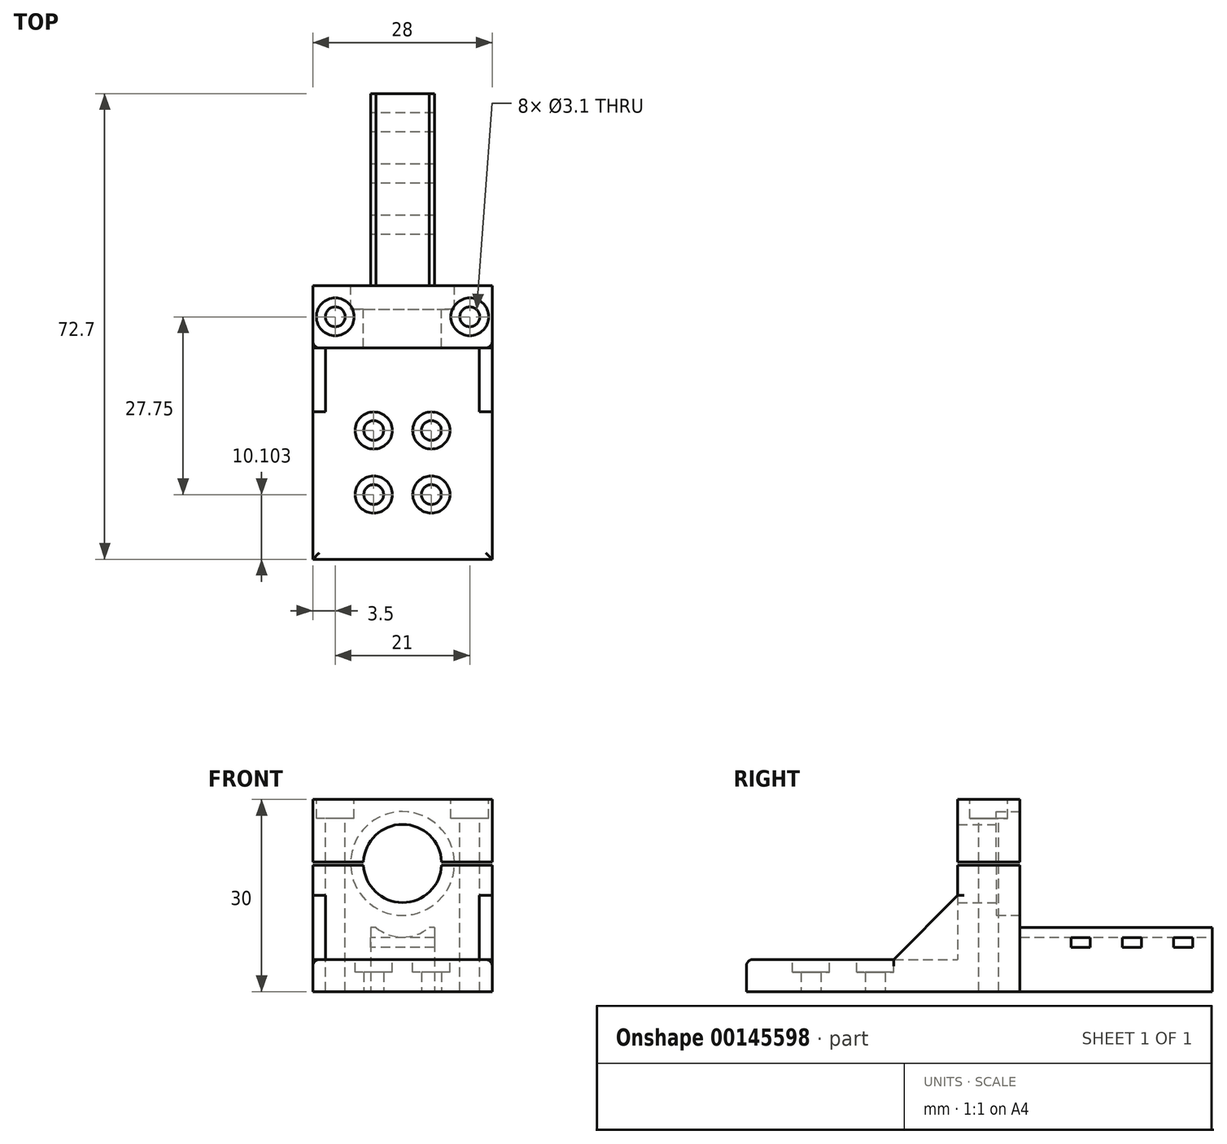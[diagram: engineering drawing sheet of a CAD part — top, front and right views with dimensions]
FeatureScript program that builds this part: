
annotation { "Feature Type Name" : "Feature", "Feature Type Description" : "" }
export const myFeature = defineFeature(function(context is Context, id is Id, definition is map)
    precondition{}
    {
        {
            var Q0;
            Q0=qCreatedBy(makeId("Top.planeOp"),FACE);
            var sketch = newSketch(context, id + "F0", { "sketchPlane" : qUnion([Q0])});
            skLineSegment(sketch, "E0", {"start": v(-14, 6.1) * mm, "end": v(-14, -26.9) * mm});
            skLineSegment(sketch, "E1", {"start": v(-14, -26.9) * mm, "end": v(14, -26.9) * mm});
            skLineSegment(sketch, "E2", {"start": v(14, -26.9) * mm, "end": v(14, 6.1) * mm});
            skLineSegment(sketch, "E3", {"start": v(14, 15.8) * mm, "end": v(-14, 15.8) * mm});
            skLineSegment(sketch, "E4.bottom", {"start": v(4.5, -6.8) * mm, "end": v(-4.5, -6.8) * mm, "construction": true});
            skLineSegment(sketch, "E4.top", {"start": v(4.5, -16.8) * mm, "end": v(-4.5, -16.8) * mm, "construction": true});
            skLineSegment(sketch, "E4.left", {"start": v(4.5, -6.8) * mm, "end": v(4.5, -16.8) * mm, "construction": true});
            skLineSegment(sketch, "E4.right", {"start": v(-4.5, -6.8) * mm, "end": v(-4.5, -16.8) * mm, "construction": true});
            skPoint(sketch, "E4.middle", {"position": v(0, -11.8) * mm});
            skCircle(sketch, "E5", {"center": v(-4.5, -6.8) * mm, "radius": 1.55 * mm});
            skCircle(sketch, "E6", {"center": v(4.5, -6.8) * mm, "radius": 1.55 * mm});
            skCircle(sketch, "E7", {"center": v(-4.5, -16.8) * mm, "radius": 1.55 * mm});
            skCircle(sketch, "E8", {"center": v(4.5, -16.8) * mm, "radius": 1.55 * mm});
            skLineSegment(sketch, "E9", {"start": v(-14, 6.1) * mm, "end": v(14, 6.1) * mm});
            skCircle(sketch, "E10", {"center": v(-10.5, 10.95) * mm, "radius": 1.3 * mm});
            skCircle(sketch, "E11", {"center": v(10.5, 10.95) * mm, "radius": 1.3 * mm});
            skLineSegment(sketch, "E12", {"start": v(-14, 6.1) * mm, "end": v(-12, 6.1) * mm});
            skLineSegment(sketch, "E13", {"start": v(-12, 6.1) * mm, "end": v(-12, -3.9) * mm});
            skLineSegment(sketch, "E14", {"start": v(-12, -3.9) * mm, "end": v(-14, -3.9) * mm});
            skLineSegment(sketch, "E15", {"start": v(14, 6.1) * mm, "end": v(12, 6.1) * mm});
            skLineSegment(sketch, "E16", {"start": v(12, 6.1) * mm, "end": v(12, -3.9) * mm});
            skLineSegment(sketch, "E17", {"start": v(12, -3.9) * mm, "end": v(14, -3.9) * mm});
            skLineSegment(sketch, "E18", {"start": v(-14, 15.8) * mm, "end": v(-14, 6.1) * mm});
            skLineSegment(sketch, "E19", {"start": v(14, 15.8) * mm, "end": v(14, 6.1) * mm});
            skPoint(sketch, "E20", {"position": v(-14, 10.95) * mm});
            skLineSegment(sketch, "E21", {"start": v(-14, 10.95) * mm, "end": v(14, 10.95) * mm, "construction": true});
            skLineSegment(sketch, "E22", {"start": v(0, 38.9) * mm, "end": v(0, -44.05) * mm, "construction": true});
            skLineSegment(sketch, "E23.bottom", {"start": v(-5, 45.8) * mm, "end": v(5, 45.8) * mm});
            skLineSegment(sketch, "E23.top", {"start": v(-5, 15.8) * mm, "end": v(5, 15.8) * mm});
            skLineSegment(sketch, "E23.left", {"start": v(-5, 45.8) * mm, "end": v(-5, 15.8) * mm});
            skLineSegment(sketch, "E23.right", {"start": v(5, 45.8) * mm, "end": v(5, 15.8) * mm});
            skPoint(sketch, "E23.middle", {"position": v(0, 30.8) * mm});
            skSolve(sketch);
        }
        {
            var Q0;
            {var subQ2=sQuery(id+"F0.wireOp",EDGE,"E1");Q0=makeQuery(id+"F0.imprint","IMPRINT",FACE,{"disambiguationData":[TD([[makeQuery(id+"F0.imprint","IMPRINT",EDGE,{"derivedFrom":subQ2}),1.0]])]});}
            var Q1;
            {var subQ2=sQuery(id+"F0.wireOp",EDGE,"E12");Q1=makeQuery(id+"F0.imprint","IMPRINT",FACE,{"disambiguationData":[TD([[makeQuery(id+"F0.imprint","IMPRINT",EDGE,{"derivedFrom":subQ2}),-1.0]])]});}
            var Q2;
            {var subQ0=sQuery(id+"F0.wireOp",EDGE,"E15");Q2=makeQuery(id+"F0.imprint","IMPRINT",FACE,{"disambiguationData":[TD([[makeQuery(id+"F0.imprint","IMPRINT",EDGE,{"derivedFrom":subQ0}),1.0]])]});}
            var Q3;
            {var subQ4=sQuery(id+"F0.wireOp",EDGE,"c3Up1kXt-IVpb-vE7n-Jt2L-Xucas93thEKn");Q3=makeQuery(id+"F0.imprint","IMPRINT",FACE,{"disambiguationData":[TD([[makeQuery(id+"F0.imprint","IMPRINT",EDGE,{"derivedFrom":subQ4}),1.0]])]});}
            var Q4;
            {var subQ4=sQuery(id+"F0.wireOp",EDGE,"E13");Q4=makeQuery(id+"F0.imprint","IMPRINT",FACE,{"disambiguationData":[TD([[makeQuery(id+"F0.imprint","IMPRINT",EDGE,{"derivedFrom":subQ4}),-1.0]])]});}
            var Q5;
            {var subQ4=sQuery(id+"F0.wireOp",EDGE,"E16");Q5=makeQuery(id+"F0.imprint","IMPRINT",FACE,{"disambiguationData":[TD([[makeQuery(id+"F0.imprint","IMPRINT",EDGE,{"derivedFrom":subQ4}),1.0]])]});}
            extrude(context, id + "F1", {"entities" : qUnion([Q0, Q1, Q2, Q3, Q4, Q5]), "depth" : 5 * mm, "offsetDistance" : 25 * mm});
        }
        {
            var Q0;
            {var subQ4=sQuery(id+"F0.wireOp",EDGE,"E13");Q0=makeQuery(id+"F0.imprint","IMPRINT",FACE,{"disambiguationData":[TD([[makeQuery(id+"F0.imprint","IMPRINT",EDGE,{"derivedFrom":subQ4}),-1.0]])]});}
            var Q1;
            {var subQ4=sQuery(id+"F0.wireOp",EDGE,"E16");Q1=makeQuery(id+"F0.imprint","IMPRINT",FACE,{"disambiguationData":[TD([[makeQuery(id+"F0.imprint","IMPRINT",EDGE,{"derivedFrom":subQ4}),1.0]])]});}
            extrude(context, id + "F2", {"entities" : qUnion([Q0, Q1]), "operationType" : NewBodyOperationType.ADD, "depth" : 15 * mm, "offsetDistance" : 25 * mm});
        }
        {
            var Q0;
            Q0=makeQuery(id+"F0.imprint","IMPRINT",FACE,{"disambiguationData":[TD([[makeQuery(id+"F0.imprint","IMPRINT",EDGE,{"derivedFrom":sQuery(id+"F0.wireOp",EDGE,"E3")}),1.0]])]});
            extrude(context, id + "F3", {"entities" : qUnion([Q0]), "operationType" : NewBodyOperationType.ADD, "depth" : 30 * mm, "offsetDistance" : 25 * mm});
        }
        {
            var Q0;
            Q0=makeQuery(id+"F3.opExtrude","SWEPT_FACE",FACE,{"disambiguationData":[OSD([sQuery(id+"F0.wireOp",EDGE,"E3")])]});
            var sketch = newSketch(context, id + "F4", { "sketchPlane" : qUnion([Q0])});
            skLineSegment(sketch, "E24", {"start": v(14, 20) * mm, "end": v(-14, 20) * mm, "construction": true});
            skPoint(sketch, "E24.endSnap0", {"position": v(-14, 15) * mm});
            skLineSegment(sketch, "E25", {"start": v(14, 20.25) * mm, "end": v(-14, 20.25) * mm});
            skLineSegment(sketch, "E26", {"start": v(14, 19.75) * mm, "end": v(-14, 19.75) * mm});
            skCircle(sketch, "E27", {"center": v(0, 20) * mm, "radius": 6.1 * mm});
            skCircle(sketch, "E28", {"center": v(0, 20) * mm, "radius": 8.1 * mm});
            skPoint(sketch, "E29.0", {"position": v(0, 0) * mm});
            skLineSegment(sketch, "E30", {"start": v(0, 0) * mm, "end": v(0, 30) * mm, "construction": true});
            skLineSegment(sketch, "E31.0", {"start": v(14, 5) * mm, "end": v(-14, 5) * mm, "construction": true});
            skSolve(sketch);
        }
        {
            var Q0;
            {var subQ0=sQuery(id+"F4.wireOp",EDGE,"E25");var subQ3=sQuery(id+"F4.wireOp",EDGE,"MANSPHcc-LTuF-cz86-WJFN-Q4U81JYctoWT");var subQ4=makeQuery(id+"F4.imprint","INTERSECT",VERTEX,{"derivedFrom":[subQ0,subQ3]});Q0=makeQuery(id+"F4.imprint","IMPRINT",FACE,{"disambiguationData":[TD([[makeQuery(id+"F4.imprint","IMPRINT",EDGE,{"disambiguationData":[TD([[subQ4,-1.0]])],"derivedFrom":subQ3}),1.0]])]});}
            var Q1;
            {var subQ0=sQuery(id+"F4.wireOp",EDGE,"E27");var subQ1=sQuery(id+"F4.wireOp",EDGE,"E25");var subQ2=makeQuery(id+"F4.imprint","INTERSECT",VERTEX,{"disambiguationData":[OD(0.0)],"derivedFrom":[subQ1,subQ0]});Q1=makeQuery(id+"F4.imprint","IMPRINT",FACE,{"disambiguationData":[TD([[makeQuery(id+"F4.imprint","IMPRINT",EDGE,{"disambiguationData":[TD([[subQ2,-1.0]])],"derivedFrom":subQ1}),-1.0]])]});}
            var Q2;
            {var subQ0=sQuery(id+"F4.wireOp",EDGE,"E27");var subQ1=sQuery(id+"F4.wireOp",EDGE,"E26");var subQ2=makeQuery(id+"F4.imprint","INTERSECT",VERTEX,{"disambiguationData":[OD(0.0)],"derivedFrom":[subQ1,subQ0]});Q2=makeQuery(id+"F4.imprint","IMPRINT",FACE,{"disambiguationData":[TD([[makeQuery(id+"F4.imprint","IMPRINT",EDGE,{"disambiguationData":[TD([[subQ2,-1.0]])],"derivedFrom":subQ1}),1.0]])]});}
            var Q3;
            {var subQ0=sQuery(id+"F4.wireOp",EDGE,"E27");var subQ1=sQuery(id+"F4.wireOp",EDGE,"E25");var subQ2=makeQuery(id+"F4.imprint","INTERSECT",VERTEX,{"disambiguationData":[OD(0.0)],"derivedFrom":[subQ1,subQ0]});Q3=makeQuery(id+"F4.imprint","IMPRINT",FACE,{"disambiguationData":[TD([[makeQuery(id+"F4.imprint","IMPRINT",EDGE,{"disambiguationData":[TD([[subQ2,-1.0]])],"derivedFrom":subQ1}),1.0]])]});}
            var Q4;
            {var subQ0=sQuery(id+"F4.wireOp",EDGE,"E25");var subQ3=sQuery(id+"F4.wireOp",EDGE,"E28");var subQ4=makeQuery(id+"F4.imprint","INTERSECT",VERTEX,{"disambiguationData":[OD(1.0)],"derivedFrom":[subQ0,subQ3]});Q4=makeQuery(id+"F4.imprint","IMPRINT",FACE,{"disambiguationData":[TD([[makeQuery(id+"F4.imprint","IMPRINT",EDGE,{"disambiguationData":[TD([[subQ4,-1.0]])],"derivedFrom":subQ3}),-1.0]])]});}
            var Q5;
            {var subQ0=sQuery(id+"F4.wireOp",EDGE,"E27");var subQ1=sQuery(id+"F4.wireOp",EDGE,"E25");var subQ2=makeQuery(id+"F4.imprint","INTERSECT",VERTEX,{"disambiguationData":[OD(1.0)],"derivedFrom":[subQ1,subQ0]});Q5=makeQuery(id+"F4.imprint","IMPRINT",FACE,{"disambiguationData":[TD([[makeQuery(id+"F4.imprint","IMPRINT",EDGE,{"disambiguationData":[TD([[subQ2,-1.0]])],"derivedFrom":subQ1}),1.0]])]});}
            var Q6;
            {var subQ0=sQuery(id+"F4.wireOp",EDGE,"E28");var subQ1=sQuery(id+"F4.wireOp",EDGE,"E25");var subQ2=makeQuery(id+"F4.imprint","INTERSECT",VERTEX,{"disambiguationData":[OD(0.0)],"derivedFrom":[subQ1,subQ0]});Q6=makeQuery(id+"F4.imprint","IMPRINT",FACE,{"disambiguationData":[TD([[makeQuery(id+"F4.imprint","IMPRINT",EDGE,{"disambiguationData":[TD([[subQ2,-1.0]])],"derivedFrom":subQ1}),1.0]])]});}
            var Q7;
            {var subQ0=sQuery(id+"F4.wireOp",EDGE,"ceOJdSXk-BByG-X7hI-yQUB-Bqh9y0oLQKFh");var subQ1=sQuery(id+"F4.wireOp",EDGE,"E25");var subQ2=makeQuery(id+"F4.imprint","INTERSECT",VERTEX,{"derivedFrom":[subQ1,subQ0]});Q7=makeQuery(id+"F4.imprint","IMPRINT",FACE,{"disambiguationData":[TD([[makeQuery(id+"F4.imprint","IMPRINT",EDGE,{"disambiguationData":[TD([[subQ2,-1.0]])],"derivedFrom":subQ1}),1.0]])]});}
            var Q8;
            {var subQ0=sQuery(id+"F4.wireOp",EDGE,"c0Dz9d9n-xce6-K6WA-Grgq-cjhxXbiWDkSi");var subQ1=sQuery(id+"F4.wireOp",EDGE,"E25");var subQ2=makeQuery(id+"F4.imprint","INTERSECT",VERTEX,{"derivedFrom":[subQ1,subQ0]});Q8=makeQuery(id+"F4.imprint","IMPRINT",FACE,{"disambiguationData":[TD([[makeQuery(id+"F4.imprint","IMPRINT",EDGE,{"disambiguationData":[TD([[subQ2,-1.0]])],"derivedFrom":subQ1}),1.0]])]});}
            var Q9;
            {var subQ0=sQuery(id+"F4.wireOp",EDGE,"MANSPHcc-LTuF-cz86-WJFN-Q4U81JYctoWT");var subQ1=sQuery(id+"F4.wireOp",EDGE,"E25");var subQ2=makeQuery(id+"F4.imprint","INTERSECT",VERTEX,{"derivedFrom":[subQ1,subQ0]});Q9=makeQuery(id+"F4.imprint","IMPRINT",FACE,{"disambiguationData":[TD([[makeQuery(id+"F4.imprint","IMPRINT",EDGE,{"disambiguationData":[TD([[subQ2,-1.0]])],"derivedFrom":subQ1}),1.0]])]});}
            extrude(context, id + "F5", {"entities" : qUnion([Q0, Q1, Q2, Q3, Q4, Q5, Q6, Q7, Q8, Q9]), "operationType" : NewBodyOperationType.REMOVE, "endBound" : BoundingType.THROUGH_ALL, "oppositeDirection" : true, "depth" : 25 * mm, "offsetDistance" : 25 * mm});
        }
        {
            var Q0;
            {var subQ0=sQuery(id+"F4.wireOp",EDGE,"E28");var subQ1=sQuery(id+"F4.wireOp",EDGE,"E25");var subQ2=makeQuery(id+"F4.imprint","INTERSECT",VERTEX,{"disambiguationData":[OD(0.0)],"derivedFrom":[subQ1,subQ0]});Q0=makeQuery(id+"F4.imprint","IMPRINT",FACE,{"disambiguationData":[TD([[makeQuery(id+"F4.imprint","IMPRINT",EDGE,{"disambiguationData":[TD([[subQ2,-1.0]])],"derivedFrom":subQ1}),-1.0]])]});}
            var Q1;
            {var subQ0=sQuery(id+"F4.wireOp",EDGE,"E28");var subQ1=sQuery(id+"F4.wireOp",EDGE,"E25");var subQ2=makeQuery(id+"F4.imprint","INTERSECT",VERTEX,{"disambiguationData":[OD(0.0)],"derivedFrom":[subQ1,subQ0]});Q1=makeQuery(id+"F4.imprint","IMPRINT",FACE,{"disambiguationData":[TD([[makeQuery(id+"F4.imprint","IMPRINT",EDGE,{"disambiguationData":[TD([[subQ2,-1.0]])],"derivedFrom":subQ1}),1.0]])]});}
            var Q2;
            {var subQ0=sQuery(id+"F4.wireOp",EDGE,"E28");var subQ1=sQuery(id+"F4.wireOp",EDGE,"E26");var subQ2=makeQuery(id+"F4.imprint","INTERSECT",VERTEX,{"disambiguationData":[OD(0.0)],"derivedFrom":[subQ1,subQ0]});Q2=makeQuery(id+"F4.imprint","IMPRINT",FACE,{"disambiguationData":[TD([[makeQuery(id+"F4.imprint","IMPRINT",EDGE,{"disambiguationData":[TD([[subQ2,-1.0]])],"derivedFrom":subQ1}),1.0]])]});}
            var Q3;
            {var subQ0=sQuery(id+"F4.wireOp",EDGE,"E27");var subQ1=sQuery(id+"F4.wireOp",EDGE,"E25");var subQ2=makeQuery(id+"F4.imprint","INTERSECT",VERTEX,{"disambiguationData":[OD(1.0)],"derivedFrom":[subQ1,subQ0]});Q3=makeQuery(id+"F4.imprint","IMPRINT",FACE,{"disambiguationData":[TD([[makeQuery(id+"F4.imprint","IMPRINT",EDGE,{"disambiguationData":[TD([[subQ2,-1.0]])],"derivedFrom":subQ1}),1.0]])]});}
            extrude(context, id + "F6", {"entities" : qUnion([Q0, Q1, Q2, Q3]), "operationType" : NewBodyOperationType.REMOVE, "oppositeDirection" : true, "depth" : 3.7 * mm, "offsetDistance" : 25 * mm});
        }
        {
            var Q0;
            Q0=makeQuery(id+"F1.opExtrude","CAP_FACE",FACE,{"disambiguationData":[OSD([sQuery(id+"F0.wireOp",EDGE,"E0"),sQuery(id+"F0.wireOp",EDGE,"E1"),sQuery(id+"F0.wireOp",EDGE,"E2"),sQuery(id+"F0.wireOp",EDGE,"E9"),sQuery(id+"F0.wireOp",EDGE,"rO4R31A8-5Sam-Peyb-ueJu-0sS9FwR46ddt"),sQuery(id+"F0.wireOp",EDGE,"Jte7CIQE-4fwr-hZTb-GItc-fUJAv9QshCUP"),sQuery(id+"F0.wireOp",EDGE,"liEgBU9Z-aVE3-jNwn-WtO9-FSSdj7A1lSbi"),sQuery(id+"F0.wireOp",EDGE,"nXXHCF9G-HeOE-aUFY-AXKT-6PfXjTbEGZXq")])],"isStart":false});
            var sketch = newSketch(context, id + "F7", { "sketchPlane" : qUnion([Q0])});
            skPoint(sketch, "E32.0", {"position": v(-4.5, -6.8) * mm});
            skPoint(sketch, "E33.0", {"position": v(4.5, -6.8) * mm});
            skPoint(sketch, "E34.0", {"position": v(4.5, -16.8) * mm});
            skPoint(sketch, "E35.0", {"position": v(-4.5, -16.8) * mm});
            skCircle(sketch, "E36", {"center": v(-4.5, -6.8) * mm, "radius": 2.9 * mm});
            skCircle(sketch, "E37", {"center": v(4.5, -6.8) * mm, "radius": 2.9 * mm});
            skCircle(sketch, "E38", {"center": v(4.5, -16.8) * mm, "radius": 2.9 * mm});
            skCircle(sketch, "E39", {"center": v(-4.5, -16.8) * mm, "radius": 2.9 * mm});
            skSolve(sketch);
        }
        {
            var Q0;
            Q0=makeQuery(id+"F7.imprint","IMPRINT",FACE,{"disambiguationData":[TD([[makeQuery(id+"F7.imprint","IMPRINT",EDGE,{"derivedFrom":sQuery(id+"F7.wireOp",EDGE,"E36")}),1.0]])]});
            var Q1;
            Q1=makeQuery(id+"F7.imprint","IMPRINT",FACE,{"disambiguationData":[TD([[makeQuery(id+"F7.imprint","IMPRINT",EDGE,{"derivedFrom":sQuery(id+"F7.wireOp",EDGE,"E37")}),1.0]])]});
            var Q2;
            Q2=makeQuery(id+"F7.imprint","IMPRINT",FACE,{"disambiguationData":[TD([[makeQuery(id+"F7.imprint","IMPRINT",EDGE,{"derivedFrom":sQuery(id+"F7.wireOp",EDGE,"E39")}),1.0]])]});
            var Q3;
            Q3=makeQuery(id+"F7.imprint","IMPRINT",FACE,{"disambiguationData":[TD([[makeQuery(id+"F7.imprint","IMPRINT",EDGE,{"derivedFrom":sQuery(id+"F7.wireOp",EDGE,"E38")}),1.0]])]});
            extrude(context, id + "F8", {"entities" : qUnion([Q0, Q1, Q2, Q3]), "operationType" : NewBodyOperationType.REMOVE, "oppositeDirection" : true, "depth" : 2 * mm, "offsetDistance" : 25 * mm});
        }
        {
            var Q0;
            Q0=makeQuery(id+"F3.opExtrude","CAP_FACE",FACE,{"disambiguationData":[OSD([sQuery(id+"F0.wireOp",EDGE,"E3"),sQuery(id+"F0.wireOp",EDGE,"E9"),sQuery(id+"F0.wireOp",EDGE,"E10"),sQuery(id+"F0.wireOp",EDGE,"E11"),sQuery(id+"F0.wireOp",EDGE,"E18"),sQuery(id+"F0.wireOp",EDGE,"E19")])],"isStart":false});
            var sketch = newSketch(context, id + "F9", { "sketchPlane" : qUnion([Q0])});
            skPoint(sketch, "E40.0", {"position": v(-10.5, 10.95) * mm});
            skPoint(sketch, "E41.0", {"position": v(10.5, 10.95) * mm});
            skCircle(sketch, "E42", {"center": v(-10.5, 10.95) * mm, "radius": 1.55 * mm});
            skCircle(sketch, "E43", {"center": v(-10.5, 10.95) * mm, "radius": 2.95 * mm});
            skCircle(sketch, "E44", {"center": v(10.5, 10.95) * mm, "radius": 1.55 * mm});
            skCircle(sketch, "E45", {"center": v(10.5, 10.95) * mm, "radius": 2.95 * mm});
            skSolve(sketch);
        }
        {
            var Q0;
            Q0=makeQuery(id+"F9.imprint","IMPRINT",FACE,{"disambiguationData":[TD([[makeQuery(id+"F9.imprint","IMPRINT",EDGE,{"derivedFrom":sQuery(id+"F9.wireOp",EDGE,"E42")}),1.0]])]});
            var Q1;
            Q1=makeQuery(id+"F9.imprint","IMPRINT",FACE,{"disambiguationData":[TD([[makeQuery(id+"F9.imprint","IMPRINT",EDGE,{"derivedFrom":sQuery(id+"F9.wireOp",EDGE,"E44")}),1.0]])]});
            extrude(context, id + "F10", {"entities" : qUnion([Q0, Q1]), "operationType" : NewBodyOperationType.REMOVE, "endBound" : BoundingType.THROUGH_ALL, "oppositeDirection" : true, "depth" : 25 * mm, "offsetDistance" : 25 * mm});
        }
        {
            var Q0;
            Q0=makeQuery(id+"F9.imprint","IMPRINT",FACE,{"disambiguationData":[TD([[makeQuery(id+"F9.imprint","IMPRINT",EDGE,{"derivedFrom":sQuery(id+"F9.wireOp",EDGE,"E42")}),-1.0]])]});
            var Q1;
            Q1=makeQuery(id+"F9.imprint","IMPRINT",FACE,{"disambiguationData":[TD([[makeQuery(id+"F9.imprint","IMPRINT",EDGE,{"derivedFrom":sQuery(id+"F9.wireOp",EDGE,"E44")}),-1.0]])]});
            extrude(context, id + "F11", {"entities" : qUnion([Q0, Q1]), "operationType" : NewBodyOperationType.REMOVE, "oppositeDirection" : true, "depth" : 3 * mm, "offsetDistance" : 25 * mm});
        }
        {
            var Q0;
            {var subQ0=sQuery(id+"F0.wireOp",EDGE,"E9");var subQ1=sQuery(id+"F0.wireOp",EDGE,"E2");var subQ2=sQuery(id+"F0.wireOp",EDGE,"E19");var subQ4=sQuery(id+"F4.wireOp",EDGE,"E25");var subQ5=makeQuery(id+"F4.imprint","INTERSECT",VERTEX,{"disambiguationData":[OD(1.0)],"derivedFrom":[subQ4,sQuery(id+"F4.wireOp",EDGE,"E28")]});Q0=makeQuery(id+"F5.boolean.opBoolean","SPLIT",EDGE,{"disambiguationData":[TD([makeQuery(id+"F5.opExtrude","SWEPT_FACE",FACE,{"disambiguationData":[OSD([subQ4]),TDD([makeQuery(id+"F4.imprint","IMPRINT",EDGE,{"disambiguationData":[TD([[makeQuery(id+"F4.imprint","INTERSECT",VERTEX,{"disambiguationData":[OD(1.0)],"derivedFrom":[subQ4,sQuery(id+"F4.wireOp",EDGE,"E27")]}),-1.0]])],"derivedFrom":subQ4}),makeQuery(id+"F4.imprint","IMPRINT",EDGE,{"disambiguationData":[TD([[subQ5,-1.0]])],"derivedFrom":subQ4})])]})])],"derivedFrom":makeQuery(id+"F3.opExtrude","SWEPT_EDGE",EDGE,{"disambiguationData":[OSD([subQ1,subQ0,subQ2])]})});}
            var Q1;
            Q1=makeQuery(id+"F1.opExtrude","CAP_EDGE",EDGE,{"disambiguationData":[OSD([sQuery(id+"F0.wireOp",EDGE,"E2")])],"isStart":false});
            var Q2;
            Q2=makeQuery(id+"F1.opExtrude","CAP_EDGE",EDGE,{"disambiguationData":[OSD([sQuery(id+"F0.wireOp",EDGE,"E0")])],"isStart":false});
            var Q3;
            Q3=makeQuery(id+"F1.opExtrude","CAP_EDGE",EDGE,{"disambiguationData":[OSD([sQuery(id+"F0.wireOp",EDGE,"E1")])],"isStart":false});
            var Q4;
            {var subQ0=sQuery(id+"F0.wireOp",EDGE,"E9");var subQ1=sQuery(id+"F0.wireOp",EDGE,"E2");var subQ2=sQuery(id+"F0.wireOp",EDGE,"E19");Q4=makeQuery(id+"F5.boolean.opBoolean","SPLIT",EDGE,{"disambiguationData":[TD([makeQuery(id+"F2.opExtrude","CAP_FACE",FACE,{"disambiguationData":[OSD([subQ1,subQ0,sQuery(id+"F0.wireOp",EDGE,"E16"),sQuery(id+"F0.wireOp",EDGE,"E17")])],"isStart":false})])],"derivedFrom":makeQuery(id+"F3.opExtrude","SWEPT_EDGE",EDGE,{"disambiguationData":[OSD([subQ1,subQ0,subQ2])]})});}
            var Q5;
            {var subQ0=sQuery(id+"F0.wireOp",EDGE,"E9");var subQ1=sQuery(id+"F0.wireOp",EDGE,"E0");var subQ2=sQuery(id+"F0.wireOp",EDGE,"E18");var subQ4=sQuery(id+"F4.wireOp",EDGE,"E25");var subQ5=makeQuery(id+"F4.imprint","INTERSECT",VERTEX,{"disambiguationData":[OD(0.0)],"derivedFrom":[subQ4,sQuery(id+"F4.wireOp",EDGE,"E28")]});Q5=makeQuery(id+"F5.boolean.opBoolean","SPLIT",EDGE,{"disambiguationData":[TD([makeQuery(id+"F5.opExtrude","SWEPT_FACE",FACE,{"disambiguationData":[OSD([subQ4]),TDD([makeQuery(id+"F4.imprint","IMPRINT",EDGE,{"disambiguationData":[TD([[subQ5,1.0]])],"derivedFrom":subQ4}),makeQuery(id+"F4.imprint","IMPRINT",EDGE,{"disambiguationData":[TD([[subQ5,-1.0]])],"derivedFrom":subQ4})])]})])],"derivedFrom":makeQuery(id+"F3.opExtrude","SWEPT_EDGE",EDGE,{"disambiguationData":[OSD([subQ1,subQ0,subQ2])]})});}
            fillet(context, id + "F12", {"entities" : qUnion([Q0, Q1, Q2, Q3, Q4, Q5]), "tangentPropagation" : true, "radius" : 1 * mm, "defaultsChanged" : true, "vertexSettings" : [], "allowEdgeOverflow" : false});
        }
        {
            var Q0;
            Q0=makeQuery(id+"F2.opExtrude","CAP_EDGE",EDGE,{"disambiguationData":[OSD([sQuery(id+"F0.wireOp",EDGE,"E14")])],"isStart":false});
            var Q1;
            Q1=makeQuery(id+"F2.opExtrude","CAP_EDGE",EDGE,{"disambiguationData":[OSD([sQuery(id+"F0.wireOp",EDGE,"E17")])],"isStart":false});
            chamfer(context, id + "F13", {"entities" : qUnion([Q0, Q1]), "width" : 10 * mm, "tangentPropagation" : true});
        }
        {
            var Q0;
            Q0=makeQuery(id+"F0.imprint","IMPRINT",FACE,{"disambiguationData":[TD([[makeQuery(id+"F0.imprint","IMPRINT",EDGE,{"derivedFrom":sQuery(id+"F0.wireOp",EDGE,"E23.bottom")}),-1.0]])]});
            extrude(context, id + "F14", {"entities" : qUnion([Q0]), "operationType" : NewBodyOperationType.ADD, "depth" : 10 * mm, "offsetDistance" : 25 * mm});
        }
        {
            var Q0;
            Q0=makeQuery(id+"F14.opExtrude","SWEPT_FACE",FACE,{"disambiguationData":[OSD([sQuery(id+"F0.wireOp",EDGE,"E23.bottom")])]});
            var sketch = newSketch(context, id + "F15", { "sketchPlane" : qUnion([Q0])});
            skPoint(sketch, "E46.0", {"position": v(0, 0) * mm});
            skLineSegment(sketch, "E47", {"start": v(0, -3.8) * mm, "end": v(0, 30.6) * mm, "construction": true});
            skCircle(sketch, "E48", {"center": v(0, 15) * mm, "radius": 6.5 * mm});
            skSolve(sketch);
        }
        {
            var Q0;
            {var subQ0=sQuery(id+"F15.wireOp",EDGE,"E48");var subQ1=makeQuery(id+"F14.opExtrude","CAP_EDGE",EDGE,{"disambiguationData":[OSD([sQuery(id+"F0.wireOp",EDGE,"E23.bottom")])],"isStart":false});var subQ2=makeQuery(id+"F15.imprint","INTERSECT",VERTEX,{"disambiguationData":[OD(0.0)],"derivedFrom":[subQ1,subQ0]});Q0=makeQuery(id+"F15.imprint","IMPRINT",FACE,{"disambiguationData":[TD([[makeQuery(id+"F15.imprint","IMPRINT",EDGE,{"disambiguationData":[TD([[subQ2,1.0]])],"derivedFrom":subQ0}),1.0]])]});}
            extrude(context, id + "F16", {"entities" : qUnion([Q0]), "operationType" : NewBodyOperationType.REMOVE, "oppositeDirection" : true, "depth" : 30 * mm, "offsetDistance" : 25 * mm});
        }
        {
            var Q0;
            Q0=makeQuery(id+"F14.opExtrude","SWEPT_FACE",FACE,{"disambiguationData":[OSD([sQuery(id+"F0.wireOp",EDGE,"E23.left")])]});
            var sketch = newSketch(context, id + "F17", { "sketchPlane" : qUnion([Q0])});
            skLineSegment(sketch, "E49", {"start": v(-48.19, 7.65) * mm, "end": v(-25.3, 7.65) * mm, "construction": true});
            skLineSegment(sketch, "E50.bottom", {"start": v(-39.8, 6.9) * mm, "end": v(-42.8, 6.9) * mm});
            skLineSegment(sketch, "E50.top", {"start": v(-39.8, 8.4) * mm, "end": v(-42.8, 8.4) * mm});
            skLineSegment(sketch, "E50.left", {"start": v(-39.8, 6.9) * mm, "end": v(-39.8, 8.4) * mm});
            skLineSegment(sketch, "E50.right", {"start": v(-42.8, 6.9) * mm, "end": v(-42.8, 8.4) * mm});
            skPoint(sketch, "E50.middle", {"position": v(-41.3, 7.65) * mm});
            skLineSegment(sketch, "E51.bottom", {"start": v(-31.8, 6.9) * mm, "end": v(-34.8, 6.9) * mm});
            skLineSegment(sketch, "E51.top", {"start": v(-31.8, 8.4) * mm, "end": v(-34.8, 8.4) * mm});
            skLineSegment(sketch, "E51.left", {"start": v(-31.8, 6.9) * mm, "end": v(-31.8, 8.4) * mm});
            skLineSegment(sketch, "E51.right", {"start": v(-34.8, 6.9) * mm, "end": v(-34.8, 8.4) * mm});
            skPoint(sketch, "E51.middle", {"position": v(-33.3, 7.65) * mm});
            skLineSegment(sketch, "E52.bottom", {"start": v(-23.8, 6.9) * mm, "end": v(-26.8, 6.9) * mm});
            skLineSegment(sketch, "E52.top", {"start": v(-23.8, 8.4) * mm, "end": v(-26.8, 8.4) * mm});
            skLineSegment(sketch, "E52.left", {"start": v(-23.8, 6.9) * mm, "end": v(-23.8, 8.4) * mm});
            skLineSegment(sketch, "E52.right", {"start": v(-26.8, 6.9) * mm, "end": v(-26.8, 8.4) * mm});
            skPoint(sketch, "E52.middle", {"position": v(-25.3, 7.65) * mm});
            skSolve(sketch);
        }
        {
            var Q0;
            Q0=makeQuery(id+"F17.imprint","IMPRINT",FACE,{"disambiguationData":[TD([[makeQuery(id+"F17.imprint","IMPRINT",EDGE,{"derivedFrom":sQuery(id+"F17.wireOp",EDGE,"E50.bottom")}),-1.0]])]});
            var Q1;
            Q1=makeQuery(id+"F17.imprint","IMPRINT",FACE,{"disambiguationData":[TD([[makeQuery(id+"F17.imprint","IMPRINT",EDGE,{"derivedFrom":sQuery(id+"F17.wireOp",EDGE,"E51.bottom")}),-1.0]])]});
            var Q2;
            Q2=makeQuery(id+"F17.imprint","IMPRINT",FACE,{"disambiguationData":[TD([[makeQuery(id+"F17.imprint","IMPRINT",EDGE,{"derivedFrom":sQuery(id+"F17.wireOp",EDGE,"E52.bottom")}),-1.0]])]});
            extrude(context, id + "F18", {"entities" : qUnion([Q0, Q1, Q2]), "operationType" : NewBodyOperationType.REMOVE, "oppositeDirection" : true, "depth" : 25 * mm, "offsetDistance" : 25 * mm});
        }
    });
